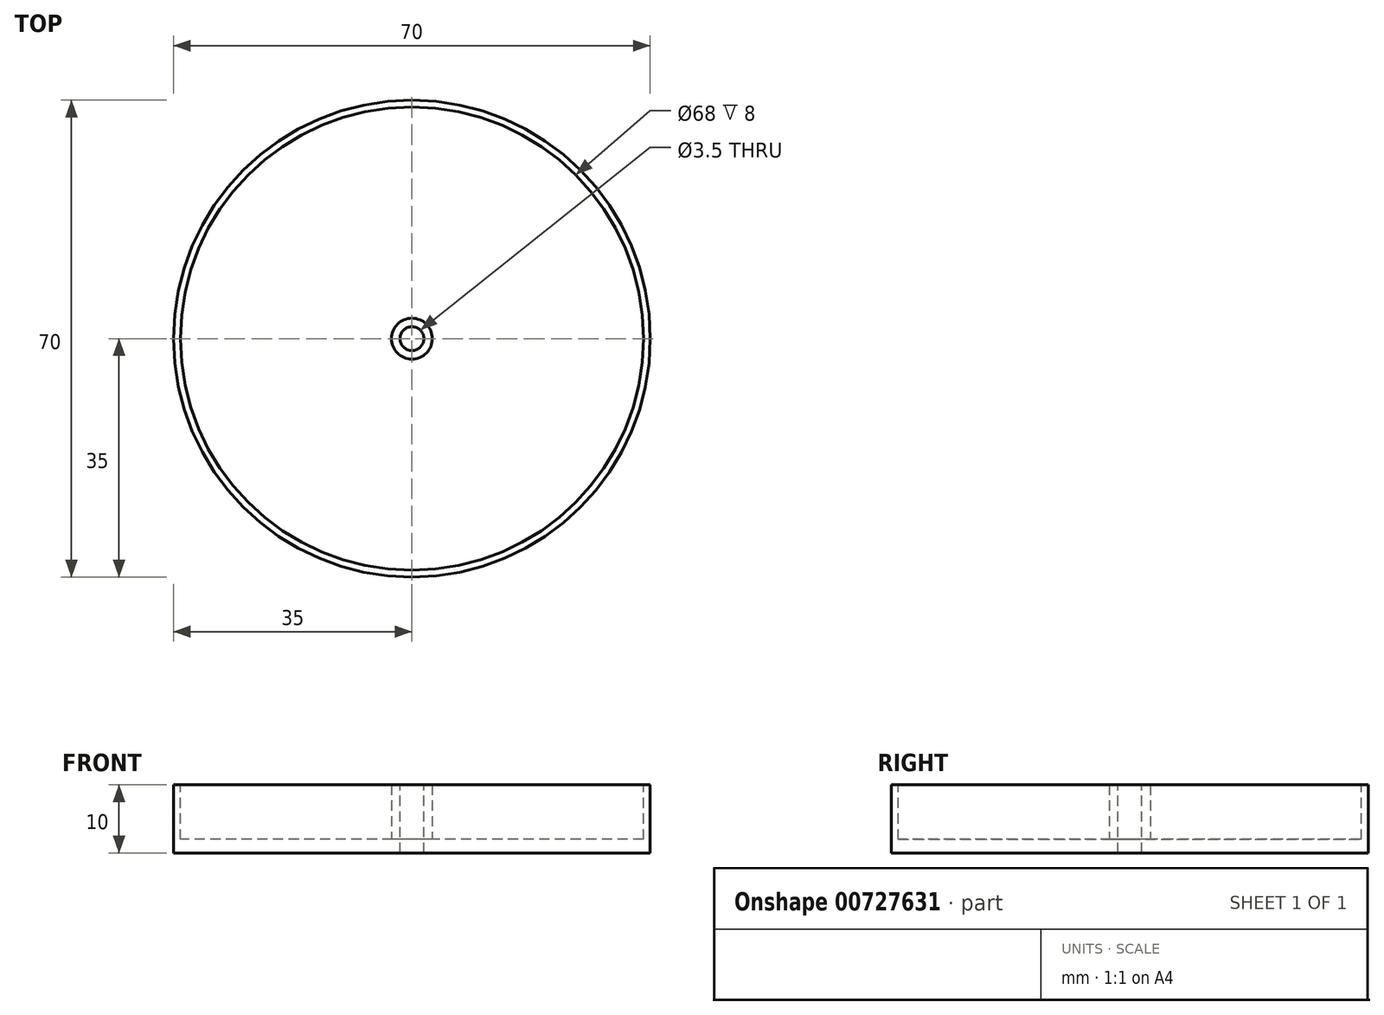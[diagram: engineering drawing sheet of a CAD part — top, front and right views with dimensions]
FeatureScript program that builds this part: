
annotation { "Feature Type Name" : "Feature", "Feature Type Description" : "" }
export const myFeature = defineFeature(function(context is Context, id is Id, definition is map)
    precondition{}
    {
        {
            var Q0;
            Q0=qCreatedBy(makeId("Top.planeOp"),FACE);
            var sketch = newSketch(context, id + "F0", { "sketchPlane" : qUnion([Q0])});
            skCircle(sketch, "E0", {"center": v(0, 0) * mm, "radius": 35 * mm});
            skSolve(sketch);
        }
        {
            var Q0;
            Q0 = qSketchRegion(id + "F0", true);
            extrude(context, id + "F1", {"entities" : qUnion([Q0]), "depth" : 10 * mm, "offsetDistance" : 25 * mm});
        }
        {
            var Q0;
            Q0=makeQuery(id+"F1.opExtrude","CAP_FACE",FACE,{"disambiguationData":[OSD([sQuery(id+"F0.wireOp",EDGE,"E0")])],"isStart":false});
            var sketch = newSketch(context, id + "F2", { "sketchPlane" : qUnion([Q0])});
            skCircle(sketch, "E1", {"center": v(0, 0) * mm, "radius": 34 * mm});
            skSolve(sketch);
        }
        {
            var Q0;
            Q0 = qSketchRegion(id + "F2", true);
            extrude(context, id + "F3", {"entities" : qUnion([Q0]), "operationType" : NewBodyOperationType.REMOVE, "oppositeDirection" : true, "depth" : 8 * mm, "offsetDistance" : 25 * mm});
        }
        {
            var Q0;
            Q0=makeQuery(id+"F3.boolean.opBoolean","COPY",FACE,{"derivedFrom":makeQuery(id+"F3.opExtrude","CAP_FACE",FACE,{"disambiguationData":[OSD([sQuery(id+"F2.wireOp",EDGE,"E1")])],"isStart":false})});
            var sketch = newSketch(context, id + "F4", { "sketchPlane" : qUnion([Q0])});
            skCircle(sketch, "E2", {"center": v(0, 0) * mm, "radius": 3 * mm});
            skSolve(sketch);
        }
        {
            var Q0;
            Q0 = qSketchRegion(id + "F4", true);
            extrude(context, id + "F5", {"entities" : qUnion([Q0]), "operationType" : NewBodyOperationType.ADD, "depth" : 8 * mm, "offsetDistance" : 25 * mm});
        }
        {
            var Q0;
            Q0=makeQuery(id+"F5.opExtrude","CAP_FACE",FACE,{"disambiguationData":[OSD([sQuery(id+"F4.wireOp",EDGE,"E2")])],"isStart":false});
            var sketch = newSketch(context, id + "F6", { "sketchPlane" : qUnion([Q0])});
            skPoint(sketch, "E3", {"position": v(0, 0) * mm});
            skSolve(sketch);
        }
        {
            var Q0;
            Q0=sQuery(id+"F6.wireOp",VERTEX,"E3");
            var Q1;
            Q1=makeQuery(id+"F1.opExtrude","SWEPT_BODY",BODY,{"disambiguationData":[OSD([sQuery(id+"F0.wireOp",EDGE,"E0")])]});
            hole(context, id + "F7", {"style" : HoleStyle.SIMPLE, "endStyle" : HoleEndStyle.THROUGH, "holeDiameter" : 3.5 * mm, "majorDiameter" : 5 * mm, "isTappedThrough" : true, "tappedDepth" : 12 * mm, "tapClearance" : 3, "locations" : qUnion([Q0]), "scope" : qUnion([Q1])});
        }
    });
